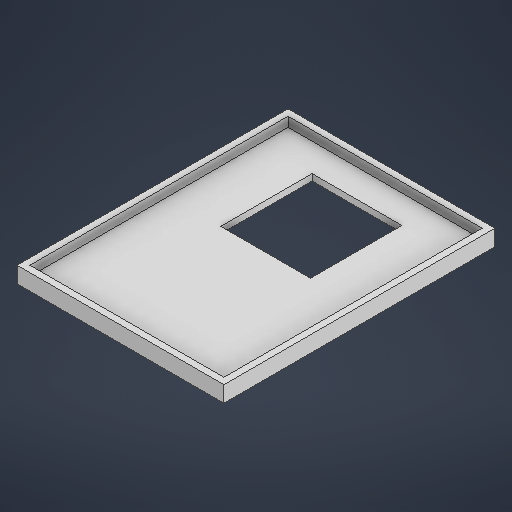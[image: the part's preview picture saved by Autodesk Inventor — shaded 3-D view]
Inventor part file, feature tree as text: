
AUTODESK INVENTOR PART (.ipt)
format: ipt  version: 2025 (Build 290162010, 162A)  size: 213,504 bytes
history: native  units: mm
features: extrude x2, sketch x1
ambient origin geometry x8: Origin, YZ Plane, XZ Plane, XY Plane, X Axis, Y Axis, Z Axis, Center Point
bodies: Solid1 (feature_tree)
feature tree (3):
  sketch  "Sketch1"  dims[d0=60.5mm d1=80.5mm d6=64.5mm d7=84.5mm d11=28.5mm d17=28.0mm d19=2.0mm d20=0.0mm d21=5.0mm d22=0.0mm]
  extrude  "Extrusion1"  Depth=80.5mm
  extrude  "Extrusion2"  Depth=64.5mm
